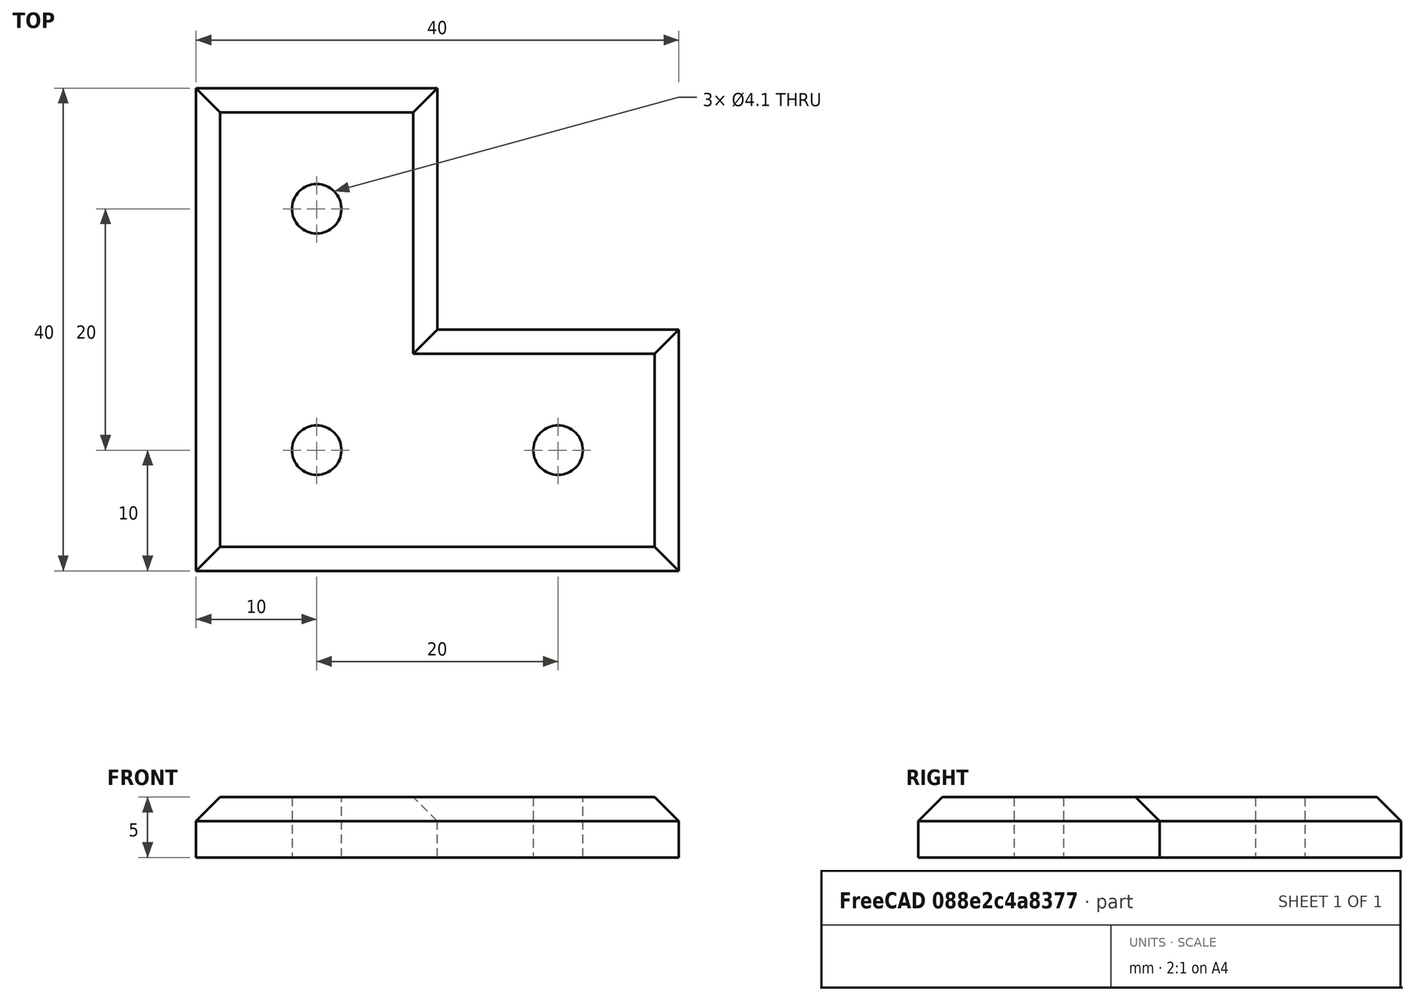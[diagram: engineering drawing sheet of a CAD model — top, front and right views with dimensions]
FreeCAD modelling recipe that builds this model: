
FCSTD DOCUMENT  (FreeCAD 0.14R3702 (Git))
Label: 2020CornerPiece
License: CC-BY 3.0
LicenseURL: http://creativecommons.org/licenses/by/3.0/
objects: Sketcher::SketchObject×1, Part::Extrusion×1, Part::Chamfer×1
note: 3 computed .brp shape members not serialized (recipe doc carries the construction recipe); baked Part::Feature solids carry a one-line shape summary decoded from their .brp

FEATURE [Sketcher::SketchObject] Sketch
  sketch-geometry (9):
    g0: LineSegment StartX=0 StartY=0 StartZ=0 EndX=0 EndY=40 EndZ=0
    g1: LineSegment StartX=0 StartY=0 StartZ=0 EndX=40 EndY=0 EndZ=0
    g2: LineSegment StartX=40 StartY=0 StartZ=0 EndX=40 EndY=20 EndZ=0
    g3: LineSegment StartX=40 StartY=20 StartZ=0 EndX=20 EndY=20 EndZ=0
    g4: LineSegment StartX=20 StartY=20 StartZ=0 EndX=20 EndY=40 EndZ=0
    g5: LineSegment StartX=0 StartY=40 StartZ=0 EndX=20 EndY=40 EndZ=0
    g6: Circle CenterX=10 CenterY=10 CenterZ=0 NormalX=0 NormalY=0 NormalZ=1 Radius=2.05
    g7: Circle CenterX=30 CenterY=10 CenterZ=0 NormalX=0 NormalY=0 NormalZ=1 Radius=2.05
    g8: Circle CenterX=10 CenterY=30 CenterZ=0 NormalX=0 NormalY=0 NormalZ=1 Radius=2.05
  constraints (14):
    c: Vertical(g0)
    c: Coincident(g1,g-1)
    c: Horizontal(g1)
    c: PointOnObject(g2,g-1)
    c: Vertical(g2)
    c: PointOnObject(g3,g2)
    c: Horizontal(g3)
    c: Coincident(g4,g3)
    c: Vertical(g4)
    c: Coincident(g5,g0)
    c: Horizontal(g5)
    c: Radius(g6) = 2.05
    c: Equal(g8,g6)
    c: Equal(g6,g7)
FEATURE [Part::Extrusion] Extrude
  Base = -> Sketch
  Dir = (0,0,5)
  Solid = true
FEATURE [Part::Chamfer] Chamfer
  Base = -> Extrude
  Edges = 6 edges r=2: [Edge4,Edge7,Edge10,Edge13,Edge16,Edge18]
